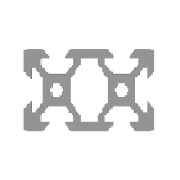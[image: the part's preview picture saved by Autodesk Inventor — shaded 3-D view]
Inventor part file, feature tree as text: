
AUTODESK INVENTOR PART (.ipt)
format: ipt  version: 2013 (Build 170138000, 138)  size: 211,968 bytes
history: native  units: mm
features: other x4, sketch x2, plane x1
ambient origin geometry x8: Origin, YZ Plane, XZ Plane, XY Plane, X Axis, Y Axis, Z Axis, Center Point
bodies: Solid1 (feature_tree), Body (feature_tree)
feature tree (7):
  other  "Driven Length"
  other  "Frame Generator"
  other  "Start Plane"
  other  "End Plane"
  sketch  "Sketch8"  dims[d2=10.0mm]
  plane  "Work Plane5"
  sketch  "Sketch9"  dims[d26=10.0mm d27=10.0mm d28=4.2mm d29=1.5mm d30=45.0deg d32=45.0deg d33=1.64mm d34=1.8mm d35=10.0mm d36=5.68mm d37=30.0mm d39=180.0deg d41=1.96mm d42=5.68mm d45=1.8mm d46=-0.0mm d47=350.0mm d48=0.13mm d49=0.0mm d54=90.0deg d51=350.0mm]
